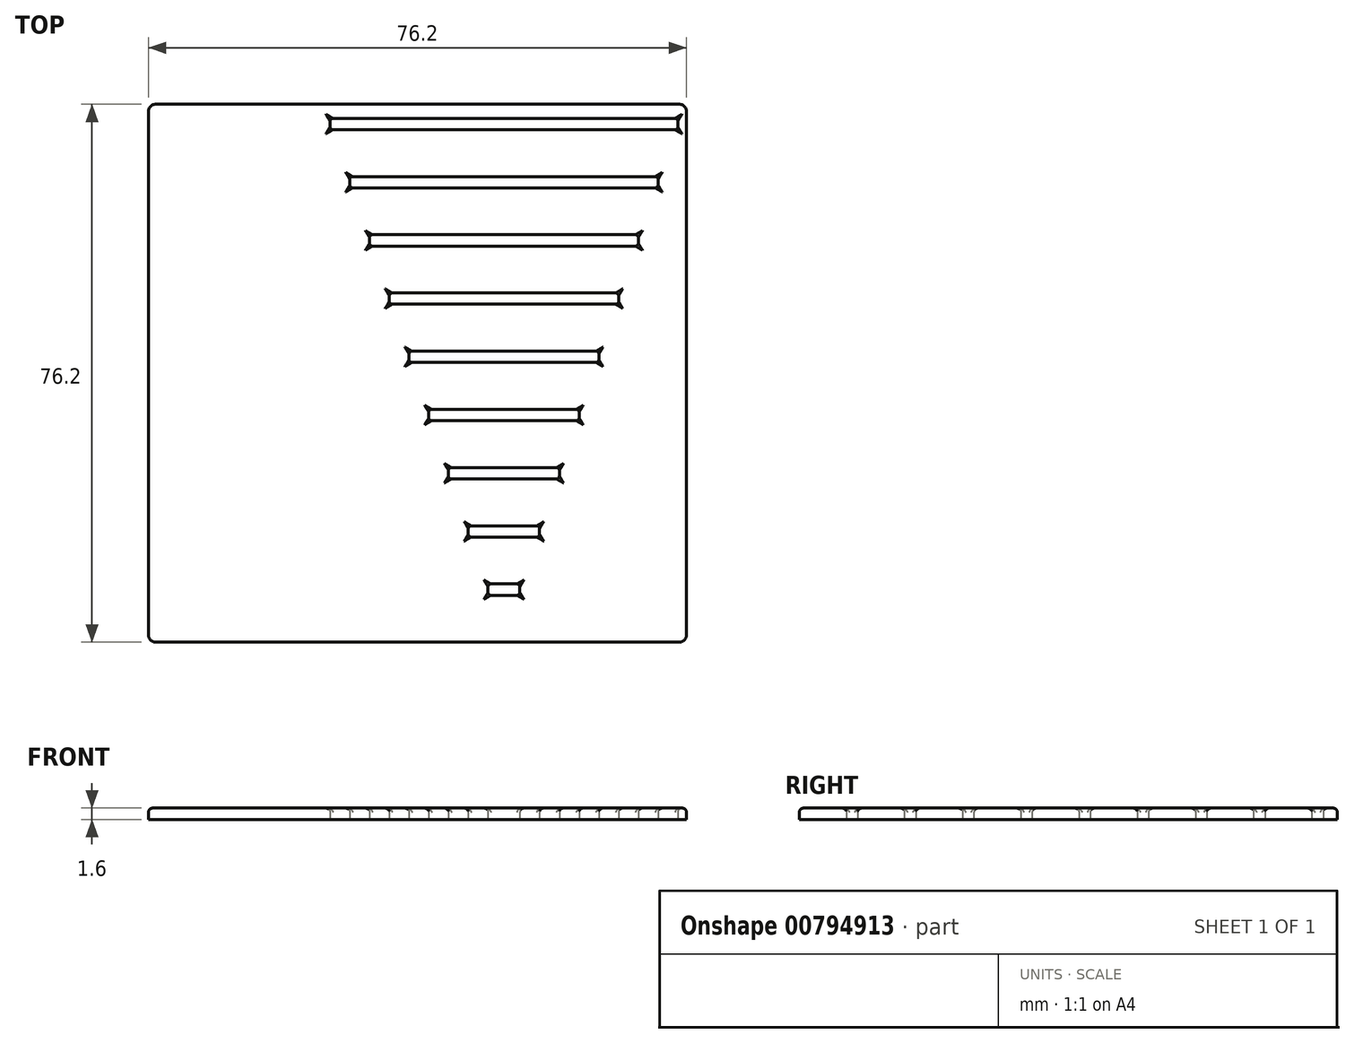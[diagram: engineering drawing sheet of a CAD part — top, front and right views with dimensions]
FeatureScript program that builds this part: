
annotation { "Feature Type Name" : "Feature", "Feature Type Description" : "" }
export const myFeature = defineFeature(function(context is Context, id is Id, definition is map)
    precondition{}
    {
        {
            var Q0;
            Q0=qCreatedBy(makeId("Top.planeOp"),FACE);
            var sketch = newSketch(context, id + "F0", { "sketchPlane" : qUnion([Q0])});
            skLineSegment(sketch, "E0.bottom", {"start": v(-38.1, 38.1) * mm, "end": v(38.1, 38.1) * mm});
            skLineSegment(sketch, "E0.top", {"start": v(-38.1, -38.1) * mm, "end": v(38.1, -38.1) * mm});
            skLineSegment(sketch, "E0.left", {"start": v(-38.1, 38.1) * mm, "end": v(-38.1, -38.1) * mm});
            skLineSegment(sketch, "E0.right", {"start": v(38.1, 38.1) * mm, "end": v(38.1, -38.1) * mm});
            skLineSegment(sketch, "E1", {"start": v(-38.1, 38.1) * mm, "end": v(38.1, -38.1) * mm, "construction": true});
            skLineSegment(sketch, "E2", {"start": v(-13.6, 38.1) * mm, "end": v(12.25, -38.1) * mm, "construction": true});
            skLineSegment(sketch, "E3", {"start": v(12.25, -38.1) * mm, "end": v(38.1, 38.1) * mm, "construction": true});
            skLineSegment(sketch, "E4.bottom", {"start": v(10, -31.46) * mm, "end": v(14.5, -31.46) * mm});
            skLineSegment(sketch, "E4.top", {"start": v(10, -29.86) * mm, "end": v(14.5, -29.86) * mm});
            skLineSegment(sketch, "E4.left", {"start": v(10, -31.46) * mm, "end": v(10, -29.86) * mm});
            skLineSegment(sketch, "E4.right", {"start": v(14.5, -31.46) * mm, "end": v(14.5, -29.86) * mm});
            skLineSegment(sketch, "E5.bottom", {"start": v(4.4, -14.97) * mm, "end": v(20.1, -14.97) * mm});
            skLineSegment(sketch, "E5.top", {"start": v(4.4, -13.37) * mm, "end": v(20.1, -13.37) * mm});
            skLineSegment(sketch, "E5.left", {"start": v(4.4, -14.97) * mm, "end": v(4.4, -13.37) * mm});
            skLineSegment(sketch, "E5.right", {"start": v(20.1, -14.97) * mm, "end": v(20.1, -13.37) * mm});
            skLineSegment(sketch, "E6.bottom", {"start": v(7.2, -23.21) * mm, "end": v(17.3, -23.21) * mm});
            skLineSegment(sketch, "E6.top", {"start": v(7.2, -21.61) * mm, "end": v(17.3, -21.61) * mm});
            skLineSegment(sketch, "E6.left", {"start": v(7.2, -23.21) * mm, "end": v(7.2, -21.61) * mm});
            skLineSegment(sketch, "E6.right", {"start": v(17.3, -23.21) * mm, "end": v(17.3, -21.61) * mm});
            skLineSegment(sketch, "E7", {"start": v(10, -38.1) * mm, "end": v(10, -31.46) * mm, "construction": true});
            skLineSegment(sketch, "E8", {"start": v(10, -29.86) * mm, "end": v(10, -23.21) * mm, "construction": true});
            skLineSegment(sketch, "E9", {"start": v(7.2, -21.61) * mm, "end": v(7.2, -14.97) * mm, "construction": true});
            skLineSegment(sketch, "E10.bottom", {"start": v(1.6, -6.72) * mm, "end": v(22.9, -6.72) * mm});
            skLineSegment(sketch, "E10.top", {"start": v(1.6, -5.12) * mm, "end": v(22.9, -5.12) * mm});
            skLineSegment(sketch, "E10.left", {"start": v(1.6, -6.72) * mm, "end": v(1.6, -5.12) * mm});
            skLineSegment(sketch, "E10.right", {"start": v(22.9, -6.72) * mm, "end": v(22.9, -5.12) * mm});
            skLineSegment(sketch, "E11", {"start": v(4.4, -13.37) * mm, "end": v(4.4, -6.72) * mm, "construction": true});
            skLineSegment(sketch, "E12.bottom", {"start": v(-1.2, 1.52) * mm, "end": v(25.7, 1.52) * mm});
            skLineSegment(sketch, "E12.top", {"start": v(-1.2, 3.12) * mm, "end": v(25.7, 3.12) * mm});
            skLineSegment(sketch, "E12.left", {"start": v(-1.2, 1.52) * mm, "end": v(-1.2, 3.12) * mm});
            skLineSegment(sketch, "E12.right", {"start": v(25.7, 1.52) * mm, "end": v(25.7, 3.12) * mm});
            skLineSegment(sketch, "E13", {"start": v(1.6, -5.12) * mm, "end": v(1.6, 1.52) * mm, "construction": true});
            skLineSegment(sketch, "E14.bottom", {"start": v(-3.99, 9.77) * mm, "end": v(28.49, 9.77) * mm});
            skLineSegment(sketch, "E14.top", {"start": v(-3.99, 11.37) * mm, "end": v(28.49, 11.37) * mm});
            skLineSegment(sketch, "E14.left", {"start": v(-3.99, 9.77) * mm, "end": v(-3.99, 11.37) * mm});
            skLineSegment(sketch, "E14.right", {"start": v(28.49, 9.77) * mm, "end": v(28.49, 11.37) * mm});
            skLineSegment(sketch, "E15.bottom", {"start": v(-6.79, 18.01) * mm, "end": v(31.29, 18.01) * mm});
            skLineSegment(sketch, "E15.top", {"start": v(-6.79, 19.61) * mm, "end": v(31.29, 19.61) * mm});
            skLineSegment(sketch, "E15.left", {"start": v(-6.79, 18.01) * mm, "end": v(-6.79, 19.61) * mm});
            skLineSegment(sketch, "E15.right", {"start": v(31.29, 18.01) * mm, "end": v(31.29, 19.61) * mm});
            skLineSegment(sketch, "E16.bottom", {"start": v(-9.58, 26.26) * mm, "end": v(34.08, 26.26) * mm});
            skLineSegment(sketch, "E16.top", {"start": v(-9.58, 27.86) * mm, "end": v(34.08, 27.86) * mm});
            skLineSegment(sketch, "E16.left", {"start": v(-9.58, 26.26) * mm, "end": v(-9.58, 27.86) * mm});
            skLineSegment(sketch, "E16.right", {"start": v(34.08, 26.26) * mm, "end": v(34.08, 27.86) * mm});
            skLineSegment(sketch, "E17.bottom", {"start": v(-12.38, 34.5) * mm, "end": v(36.88, 34.5) * mm});
            skLineSegment(sketch, "E17.top", {"start": v(-12.38, 36.1) * mm, "end": v(36.88, 36.1) * mm});
            skLineSegment(sketch, "E17.left", {"start": v(-12.38, 34.5) * mm, "end": v(-12.38, 36.1) * mm});
            skLineSegment(sketch, "E17.right", {"start": v(36.88, 34.5) * mm, "end": v(36.88, 36.1) * mm});
            skLineSegment(sketch, "E18", {"start": v(-1.2, 3.12) * mm, "end": v(-1.2, 9.77) * mm, "construction": true});
            skLineSegment(sketch, "E19", {"start": v(-3.99, 11.37) * mm, "end": v(-3.99, 18.01) * mm, "construction": true});
            skLineSegment(sketch, "E20", {"start": v(-6.79, 19.61) * mm, "end": v(-6.79, 26.26) * mm, "construction": true});
            skLineSegment(sketch, "E21", {"start": v(-9.58, 27.86) * mm, "end": v(-9.58, 34.5) * mm, "construction": true});
            skLineSegment(sketch, "E22", {"start": v(-12.38, 36.1) * mm, "end": v(-12.38, 38.1) * mm, "construction": true});
            skLineSegment(sketch, "E23", {"start": v(-13.6, 38.1) * mm, "end": v(-13.6, -38.1) * mm, "construction": true});
            skSolve(sketch);
        }
        {
            var Q0;
            Q0=makeQuery(id+"F0.imprint","IMPRINT",FACE,{"disambiguationData":[TD([[makeQuery(id+"F0.imprint","IMPRINT",EDGE,{"derivedFrom":sQuery(id+"F0.wireOp",EDGE,"E0.bottom")}),-1.0]])]});
            extrude(context, id + "F1", {"entities" : qUnion([Q0]), "depth" : 1.6 * mm, "offsetDistance" : 25 * mm});
        }
        {
            var Q0;
            Q0=makeQuery(id+"F1.opExtrude","CAP_FACE",FACE,{"disambiguationData":[OSD([sQuery(id+"F0.wireOp",EDGE,"E0.bottom"),sQuery(id+"F0.wireOp",EDGE,"E0.top"),sQuery(id+"F0.wireOp",EDGE,"E0.left"),sQuery(id+"F0.wireOp",EDGE,"E0.right"),sQuery(id+"F0.wireOp",EDGE,"E4.bottom"),sQuery(id+"F0.wireOp",EDGE,"E4.top"),sQuery(id+"F0.wireOp",EDGE,"E4.left"),sQuery(id+"F0.wireOp",EDGE,"E4.right"),sQuery(id+"F0.wireOp",EDGE,"E5.bottom"),sQuery(id+"F0.wireOp",EDGE,"E5.top"),sQuery(id+"F0.wireOp",EDGE,"E5.left"),sQuery(id+"F0.wireOp",EDGE,"E5.right"),sQuery(id+"F0.wireOp",EDGE,"E6.bottom"),sQuery(id+"F0.wireOp",EDGE,"E6.top"),sQuery(id+"F0.wireOp",EDGE,"E6.left"),sQuery(id+"F0.wireOp",EDGE,"E6.right"),sQuery(id+"F0.wireOp",EDGE,"E10.bottom"),sQuery(id+"F0.wireOp",EDGE,"E10.top"),sQuery(id+"F0.wireOp",EDGE,"E10.left"),sQuery(id+"F0.wireOp",EDGE,"E10.right"),sQuery(id+"F0.wireOp",EDGE,"E12.bottom"),sQuery(id+"F0.wireOp",EDGE,"E12.top"),sQuery(id+"F0.wireOp",EDGE,"E12.left"),sQuery(id+"F0.wireOp",EDGE,"E12.right")])],"isStart":false});
            fillet(context, id + "F2", {"entities" : qUnion([Q0]), "radius" : 0.6 * mm, "tangentPropagation" : true, "allowEdgeOverflow" : false});
        }
        {
            var Q0;
            Q0=makeQuery(id+"F1.opExtrude","SWEPT_EDGE",EDGE,{"disambiguationData":[OSD([sQuery(id+"F0.wireOp",EDGE,"E10.bottom"),sQuery(id+"F0.wireOp",EDGE,"E10.right")])]});
            var Q1;
            Q1=makeQuery(id+"F1.opExtrude","SWEPT_EDGE",EDGE,{"disambiguationData":[OSD([sQuery(id+"F0.wireOp",EDGE,"E5.bottom"),sQuery(id+"F0.wireOp",EDGE,"E5.right")])]});
            var Q2;
            Q2=makeQuery(id+"F1.opExtrude","SWEPT_EDGE",EDGE,{"disambiguationData":[OSD([sQuery(id+"F0.wireOp",EDGE,"E6.bottom"),sQuery(id+"F0.wireOp",EDGE,"E6.right")])]});
            var Q3;
            Q3=makeQuery(id+"F1.opExtrude","SWEPT_EDGE",EDGE,{"disambiguationData":[OSD([sQuery(id+"F0.wireOp",EDGE,"E4.bottom"),sQuery(id+"F0.wireOp",EDGE,"E4.right")])]});
            var Q4;
            Q4=makeQuery(id+"F1.opExtrude","SWEPT_EDGE",EDGE,{"disambiguationData":[OSD([sQuery(id+"F0.wireOp",EDGE,"E6.top"),sQuery(id+"F0.wireOp",EDGE,"E6.right")])]});
            var Q5;
            Q5=makeQuery(id+"F1.opExtrude","SWEPT_EDGE",EDGE,{"disambiguationData":[OSD([sQuery(id+"F0.wireOp",EDGE,"E5.top"),sQuery(id+"F0.wireOp",EDGE,"E5.right")])]});
            var Q6;
            Q6=makeQuery(id+"F1.opExtrude","SWEPT_EDGE",EDGE,{"disambiguationData":[OSD([sQuery(id+"F0.wireOp",EDGE,"E10.top"),sQuery(id+"F0.wireOp",EDGE,"E10.right")])]});
            var Q7;
            Q7=makeQuery(id+"F1.opExtrude","SWEPT_EDGE",EDGE,{"disambiguationData":[OSD([sQuery(id+"F0.wireOp",EDGE,"E12.top"),sQuery(id+"F0.wireOp",EDGE,"E12.right")])]});
            var Q8;
            Q8=makeQuery(id+"F1.opExtrude","SWEPT_EDGE",EDGE,{"disambiguationData":[OSD([sQuery(id+"F0.wireOp",EDGE,"E4.top"),sQuery(id+"F0.wireOp",EDGE,"E4.right")])]});
            var Q9;
            Q9=makeQuery(id+"F1.opExtrude","SWEPT_EDGE",EDGE,{"disambiguationData":[OSD([sQuery(id+"F0.wireOp",EDGE,"E12.top"),sQuery(id+"F0.wireOp",EDGE,"E12.left")])]});
            var Q10;
            Q10=makeQuery(id+"F1.opExtrude","SWEPT_EDGE",EDGE,{"disambiguationData":[OSD([sQuery(id+"F0.wireOp",EDGE,"E10.top"),sQuery(id+"F0.wireOp",EDGE,"E10.left")])]});
            var Q11;
            Q11=makeQuery(id+"F1.opExtrude","SWEPT_EDGE",EDGE,{"disambiguationData":[OSD([sQuery(id+"F0.wireOp",EDGE,"E5.top"),sQuery(id+"F0.wireOp",EDGE,"E5.left")])]});
            var Q12;
            Q12=makeQuery(id+"F1.opExtrude","SWEPT_EDGE",EDGE,{"disambiguationData":[OSD([sQuery(id+"F0.wireOp",EDGE,"E6.top"),sQuery(id+"F0.wireOp",EDGE,"E6.left")])]});
            var Q13;
            Q13=makeQuery(id+"F1.opExtrude","SWEPT_EDGE",EDGE,{"disambiguationData":[OSD([sQuery(id+"F0.wireOp",EDGE,"E4.top"),sQuery(id+"F0.wireOp",EDGE,"E4.left")])]});
            var Q14;
            Q14=makeQuery(id+"F1.opExtrude","SWEPT_EDGE",EDGE,{"disambiguationData":[OSD([sQuery(id+"F0.wireOp",EDGE,"E6.bottom"),sQuery(id+"F0.wireOp",EDGE,"E6.left")])]});
            var Q15;
            Q15=makeQuery(id+"F1.opExtrude","SWEPT_EDGE",EDGE,{"disambiguationData":[OSD([sQuery(id+"F0.wireOp",EDGE,"E5.bottom"),sQuery(id+"F0.wireOp",EDGE,"E5.left")])]});
            var Q16;
            Q16=makeQuery(id+"F1.opExtrude","SWEPT_EDGE",EDGE,{"disambiguationData":[OSD([sQuery(id+"F0.wireOp",EDGE,"E10.bottom"),sQuery(id+"F0.wireOp",EDGE,"E10.left")])]});
            var Q17;
            Q17=makeQuery(id+"F1.opExtrude","SWEPT_EDGE",EDGE,{"disambiguationData":[OSD([sQuery(id+"F0.wireOp",EDGE,"E12.bottom"),sQuery(id+"F0.wireOp",EDGE,"E12.left")])]});
            var Q18;
            Q18=makeQuery(id+"F1.opExtrude","SWEPT_EDGE",EDGE,{"disambiguationData":[OSD([sQuery(id+"F0.wireOp",EDGE,"E4.bottom"),sQuery(id+"F0.wireOp",EDGE,"E4.left")])]});
            var Q19;
            Q19=makeQuery(id+"F1.opExtrude","SWEPT_EDGE",EDGE,{"disambiguationData":[OSD([sQuery(id+"F0.wireOp",EDGE,"E12.bottom"),sQuery(id+"F0.wireOp",EDGE,"E12.right")])]});
            var Q20;
            Q20=makeQuery(id+"F1.opExtrude","SWEPT_EDGE",EDGE,{"disambiguationData":[OSD([sQuery(id+"F0.wireOp",EDGE,"E14.bottom"),sQuery(id+"F0.wireOp",EDGE,"E14.right")])]});
            var Q21;
            Q21=makeQuery(id+"F1.opExtrude","SWEPT_EDGE",EDGE,{"disambiguationData":[OSD([sQuery(id+"F0.wireOp",EDGE,"E14.top"),sQuery(id+"F0.wireOp",EDGE,"E14.right")])]});
            var Q22;
            Q22=makeQuery(id+"F1.opExtrude","SWEPT_EDGE",EDGE,{"disambiguationData":[OSD([sQuery(id+"F0.wireOp",EDGE,"E16.top"),sQuery(id+"F0.wireOp",EDGE,"E16.right")])]});
            var Q23;
            Q23=makeQuery(id+"F1.opExtrude","SWEPT_EDGE",EDGE,{"disambiguationData":[OSD([sQuery(id+"F0.wireOp",EDGE,"E16.bottom"),sQuery(id+"F0.wireOp",EDGE,"E16.right")])]});
            var Q24;
            Q24=makeQuery(id+"F1.opExtrude","SWEPT_EDGE",EDGE,{"disambiguationData":[OSD([sQuery(id+"F0.wireOp",EDGE,"E15.bottom"),sQuery(id+"F0.wireOp",EDGE,"E15.right")])]});
            var Q25;
            Q25=makeQuery(id+"F1.opExtrude","SWEPT_EDGE",EDGE,{"disambiguationData":[OSD([sQuery(id+"F0.wireOp",EDGE,"E15.top"),sQuery(id+"F0.wireOp",EDGE,"E15.right")])]});
            var Q26;
            Q26=makeQuery(id+"F1.opExtrude","SWEPT_EDGE",EDGE,{"disambiguationData":[OSD([sQuery(id+"F0.wireOp",EDGE,"E17.top"),sQuery(id+"F0.wireOp",EDGE,"E17.right")])]});
            var Q27;
            Q27=makeQuery(id+"F1.opExtrude","SWEPT_EDGE",EDGE,{"disambiguationData":[OSD([sQuery(id+"F0.wireOp",EDGE,"E17.bottom"),sQuery(id+"F0.wireOp",EDGE,"E17.right")])]});
            var Q28;
            Q28=makeQuery(id+"F1.opExtrude","SWEPT_EDGE",EDGE,{"disambiguationData":[OSD([sQuery(id+"F0.wireOp",EDGE,"E17.top"),sQuery(id+"F0.wireOp",EDGE,"E17.left")])]});
            var Q29;
            Q29=makeQuery(id+"F1.opExtrude","SWEPT_EDGE",EDGE,{"disambiguationData":[OSD([sQuery(id+"F0.wireOp",EDGE,"E17.bottom"),sQuery(id+"F0.wireOp",EDGE,"E17.left")])]});
            var Q30;
            Q30=makeQuery(id+"F1.opExtrude","SWEPT_EDGE",EDGE,{"disambiguationData":[OSD([sQuery(id+"F0.wireOp",EDGE,"E16.bottom"),sQuery(id+"F0.wireOp",EDGE,"E16.left")])]});
            var Q31;
            Q31=makeQuery(id+"F1.opExtrude","SWEPT_EDGE",EDGE,{"disambiguationData":[OSD([sQuery(id+"F0.wireOp",EDGE,"E15.bottom"),sQuery(id+"F0.wireOp",EDGE,"E15.left")])]});
            var Q32;
            Q32=makeQuery(id+"F1.opExtrude","SWEPT_EDGE",EDGE,{"disambiguationData":[OSD([sQuery(id+"F0.wireOp",EDGE,"E15.top"),sQuery(id+"F0.wireOp",EDGE,"E15.left")])]});
            var Q33;
            Q33=makeQuery(id+"F1.opExtrude","SWEPT_EDGE",EDGE,{"disambiguationData":[OSD([sQuery(id+"F0.wireOp",EDGE,"E16.top"),sQuery(id+"F0.wireOp",EDGE,"E16.left")])]});
            var Q34;
            Q34=makeQuery(id+"F1.opExtrude","SWEPT_EDGE",EDGE,{"disambiguationData":[OSD([sQuery(id+"F0.wireOp",EDGE,"E14.top"),sQuery(id+"F0.wireOp",EDGE,"E14.left")])]});
            var Q35;
            Q35=makeQuery(id+"F1.opExtrude","SWEPT_EDGE",EDGE,{"disambiguationData":[OSD([sQuery(id+"F0.wireOp",EDGE,"E14.bottom"),sQuery(id+"F0.wireOp",EDGE,"E14.left")])]});
            fillet(context, id + "F3", {"entities" : qUnion([Q0, Q1, Q2, Q3, Q4, Q5, Q6, Q7, Q8, Q9, Q10, Q11, Q12, Q13, Q14, Q15, Q16, Q17, Q18, Q19, Q20, Q21, Q22, Q23, Q24, Q25, Q26, Q27, Q28, Q29, Q30, Q31, Q32, Q33, Q34, Q35]), "radius" : 0.4 * mm, "tangentPropagation" : true, "allowEdgeOverflow" : false});
        }
        {
            var Q0;
            Q0=makeQuery(id+"F1.opExtrude","SWEPT_EDGE",EDGE,{"disambiguationData":[OSD([sQuery(id+"F0.wireOp",EDGE,"E0.bottom"),sQuery(id+"F0.wireOp",EDGE,"E0.right")])]});
            var Q1;
            Q1=makeQuery(id+"F1.opExtrude","SWEPT_EDGE",EDGE,{"disambiguationData":[OSD([sQuery(id+"F0.wireOp",EDGE,"E0.top"),sQuery(id+"F0.wireOp",EDGE,"E0.right")])]});
            var Q2;
            Q2=makeQuery(id+"F1.opExtrude","SWEPT_EDGE",EDGE,{"disambiguationData":[OSD([sQuery(id+"F0.wireOp",EDGE,"E0.top"),sQuery(id+"F0.wireOp",EDGE,"E0.left")])]});
            var Q3;
            Q3=makeQuery(id+"F1.opExtrude","SWEPT_EDGE",EDGE,{"disambiguationData":[OSD([sQuery(id+"F0.wireOp",EDGE,"E0.bottom"),sQuery(id+"F0.wireOp",EDGE,"E0.left")])]});
            fillet(context, id + "F4", {"entities" : qUnion([Q0, Q1, Q2, Q3]), "radius" : 1 * mm, "tangentPropagation" : true, "allowEdgeOverflow" : false});
        }
    });
